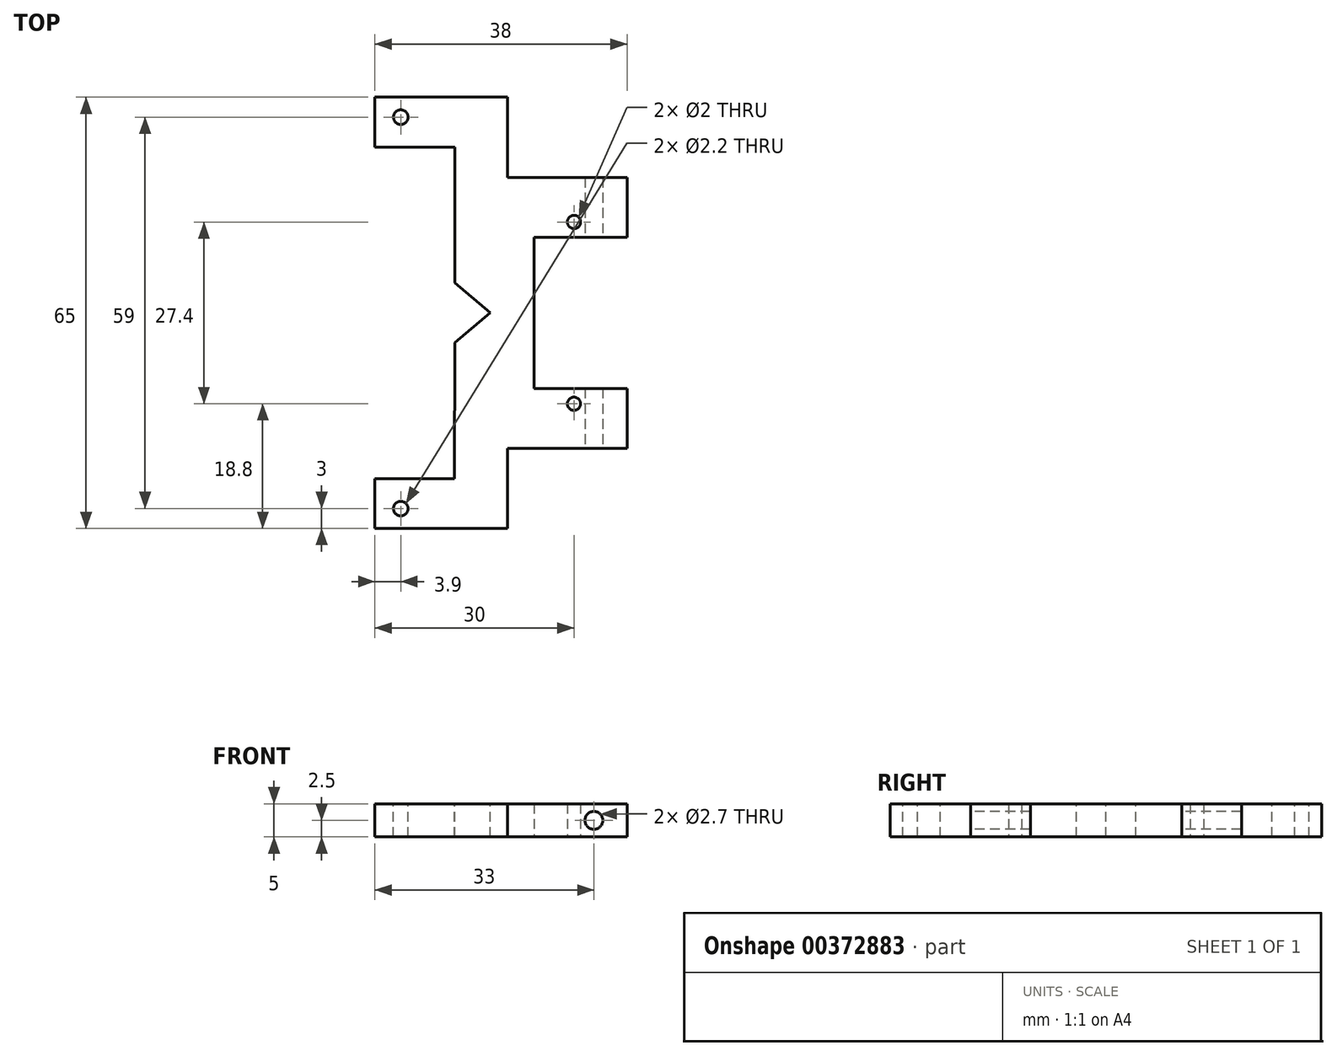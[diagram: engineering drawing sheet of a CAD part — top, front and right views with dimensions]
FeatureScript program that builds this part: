
annotation { "Feature Type Name" : "Feature", "Feature Type Description" : "" }
export const myFeature = defineFeature(function(context is Context, id is Id, definition is map)
    precondition{}
    {
        {
            var Q0;
            Q0=qCreatedBy(makeId("Top.planeOp"),FACE);
            var sketch = newSketch(context, id + "F0", { "sketchPlane" : qUnion([Q0])});
            skLineSegment(sketch, "E0.bottom", {"start": v(-7, 11.4) * mm, "end": v(7, 11.4) * mm});
            skLineSegment(sketch, "E0.top", {"start": v(-7, -11.4) * mm, "end": v(7, -11.4) * mm});
            skLineSegment(sketch, "E0.left", {"start": v(-7, 11.4) * mm, "end": v(-7, -11.4) * mm});
            skLineSegment(sketch, "E1", {"start": v(-7, 11.4) * mm, "end": v(7, -11.4) * mm, "construction": true});
            skLineSegment(sketch, "E2.0", {"start": v(-11, 20.4) * mm, "end": v(7, 20.4) * mm});
            skLineSegment(sketch, "E2.1", {"start": v(-11, 20.4) * mm, "end": v(-11, -20.4) * mm});
            skLineSegment(sketch, "E2.2", {"start": v(-11, -20.4) * mm, "end": v(7, -20.4) * mm});
            skLineSegment(sketch, "E3", {"start": v(7, 11.4) * mm, "end": v(7, 20.4) * mm});
            skLineSegment(sketch, "E4", {"start": v(7, -20.4) * mm, "end": v(7, -11.4) * mm});
            skCircle(sketch, "E5", {"center": v(-1, -13.7) * mm, "radius": 1 * mm});
            skLineSegment(sketch, "E6", {"start": v(-24.45, 0) * mm, "end": v(24.55, 0) * mm, "construction": true});
            skCircle(sketch, "E7.MirrorC", {"center": v(-1, 13.7) * mm, "radius": 1 * mm});
            skSolve(sketch);
        }
        {
            var Q0;
            Q0=makeQuery(id+"F0.imprint","IMPRINT",FACE,{"disambiguationData":[TD([[makeQuery(id+"F0.imprint","IMPRINT",EDGE,{"derivedFrom":sQuery(id+"F0.wireOp",EDGE,"E0.bottom")}),1.0]])]});
            extrude(context, id + "F1", {"entities" : qUnion([Q0]), "endBound" : BoundingType.SYMMETRIC, "depth" : 5 * mm, "offsetDistance" : 25 * mm});
        }
        {
            var Q0;
            Q0=qCreatedBy(makeId("Front.planeOp"),FACE);
            var sketch = newSketch(context, id + "F2", { "sketchPlane" : qUnion([Q0])});
            skLineSegment(sketch, "E8", {"start": v(2, 0) * mm, "end": v(2, 0) * mm});
            skCircle(sketch, "E9", {"center": v(2, 0) * mm, "radius": 1.35 * mm});
            skLineSegment(sketch, "E10", {"start": v(0, 0) * mm, "end": v(2, 0) * mm});
            skSolve(sketch);
        }
        {
            var Q0;
            Q0 = qSketchRegion(id + "F2", true);
            var Q1;
            Q1=makeQuery(id+"F1.opExtrude","SWEPT_BODY",BODY,{"disambiguationData":[OSD([sQuery(id+"F0.wireOp",EDGE,"E0.bottom"),sQuery(id+"F0.wireOp",EDGE,"E0.top"),sQuery(id+"F0.wireOp",EDGE,"E0.left"),sQuery(id+"F0.wireOp",EDGE,"E2.0"),sQuery(id+"F0.wireOp",EDGE,"E2.1"),sQuery(id+"F0.wireOp",EDGE,"E2.2"),sQuery(id+"F0.wireOp",EDGE,"E3"),sQuery(id+"F0.wireOp",EDGE,"E4")])]});
            extrude(context, id + "F3", {"entities" : qUnion([Q0]), "operationType" : NewBodyOperationType.REMOVE, "endBound" : BoundingType.SYMMETRIC, "oppositeDirection" : true, "depth" : 50 * mm, "endBoundEntityBody" : qUnion([Q1]), "offsetDistance" : 25 * mm});
        }
        {
            var Q0;
            Q0=makeQuery(id+"F1.opExtrude","CAP_FACE",FACE,{"disambiguationData":[OSD([sQuery(id+"F0.wireOp",EDGE,"E0.bottom"),sQuery(id+"F0.wireOp",EDGE,"E0.top"),sQuery(id+"F0.wireOp",EDGE,"E0.left"),sQuery(id+"F0.wireOp",EDGE,"E2.0"),sQuery(id+"F0.wireOp",EDGE,"E2.1"),sQuery(id+"F0.wireOp",EDGE,"E2.2"),sQuery(id+"F0.wireOp",EDGE,"E3"),sQuery(id+"F0.wireOp",EDGE,"E4")])],"isStart":false});
            cPlane(context, id + "F4", {"entities" : qUnion([Q0]), "cplaneType" : CPlaneType.OFFSET, "offset" : 0 * mm, "width" : 150 * mm, "height" : 150 * mm});
        }
        {
            var Q0;
            Q0=qCreatedBy(id+"F4.planeOp",FACE);
            var sketch = newSketch(context, id + "F5", { "sketchPlane" : qUnion([Q0])});
            skLineSegment(sketch, "E11.bottom", {"start": v(-31, -32.5) * mm, "end": v(-11, -32.5) * mm});
            skLineSegment(sketch, "E12.MirrorCS", {"start": v(-31, 32.5) * mm, "end": v(-11, 32.5) * mm});
            skLineSegment(sketch, "E13", {"start": v(-31, -32.5) * mm, "end": v(-31, -25) * mm});
            skLineSegment(sketch, "E14", {"start": v(-11, -32.5) * mm, "end": v(-11, 32.5) * mm});
            skLineSegment(sketch, "E15.bottom", {"start": v(-31, -25) * mm, "end": v(-19, -25) * mm});
            skLineSegment(sketch, "E15.top", {"start": v(-31, 25) * mm, "end": v(-18.93, 25) * mm});
            skLineSegment(sketch, "E15.right", {"start": v(-19, -25) * mm, "end": v(-18.97, -4.49) * mm});
            skLineSegment(sketch, "E16.trimOffspring", {"start": v(-31, 25) * mm, "end": v(-31, 32.5) * mm});
            skLineSegment(sketch, "E17", {"start": v(-18.97, -4.49) * mm, "end": v(-13.6, 0) * mm});
            skLineSegment(sketch, "E18", {"start": v(-13.6, 0) * mm, "end": v(-18.96, 4.5) * mm});
            skLineSegment(sketch, "E19.trimOffspring", {"start": v(-18.96, 4.5) * mm, "end": v(-18.93, 25) * mm});
            skSolve(sketch);
        }
        {
            var Q0;
            Q0 = qSketchRegion(id + "F5", true);
            extrude(context, id + "F6", {"entities" : qUnion([Q0]), "operationType" : NewBodyOperationType.ADD, "oppositeDirection" : true, "depth" : 5 * mm, "offsetDistance" : 25 * mm});
        }
        {
            var Q0;
            Q0=qCreatedBy(id+"F4.planeOp",FACE);
            var sketch = newSketch(context, id + "F7", { "sketchPlane" : qUnion([Q0])});
            skCircle(sketch, "E20", {"center": v(-27.1, 29.5) * mm, "radius": 1.1 * mm});
            skCircle(sketch, "E21.MirrorC", {"center": v(-27.1, -29.5) * mm, "radius": 1.1 * mm});
            skSolve(sketch);
        }
        {
            var Q0;
            Q0 = qSketchRegion(id + "F7", true);
            extrude(context, id + "F8", {"entities" : qUnion([Q0]), "operationType" : NewBodyOperationType.REMOVE, "endBound" : BoundingType.UP_TO_NEXT, "oppositeDirection" : true, "depth" : 5 * mm, "offsetDistance" : 25 * mm});
        }
    });
